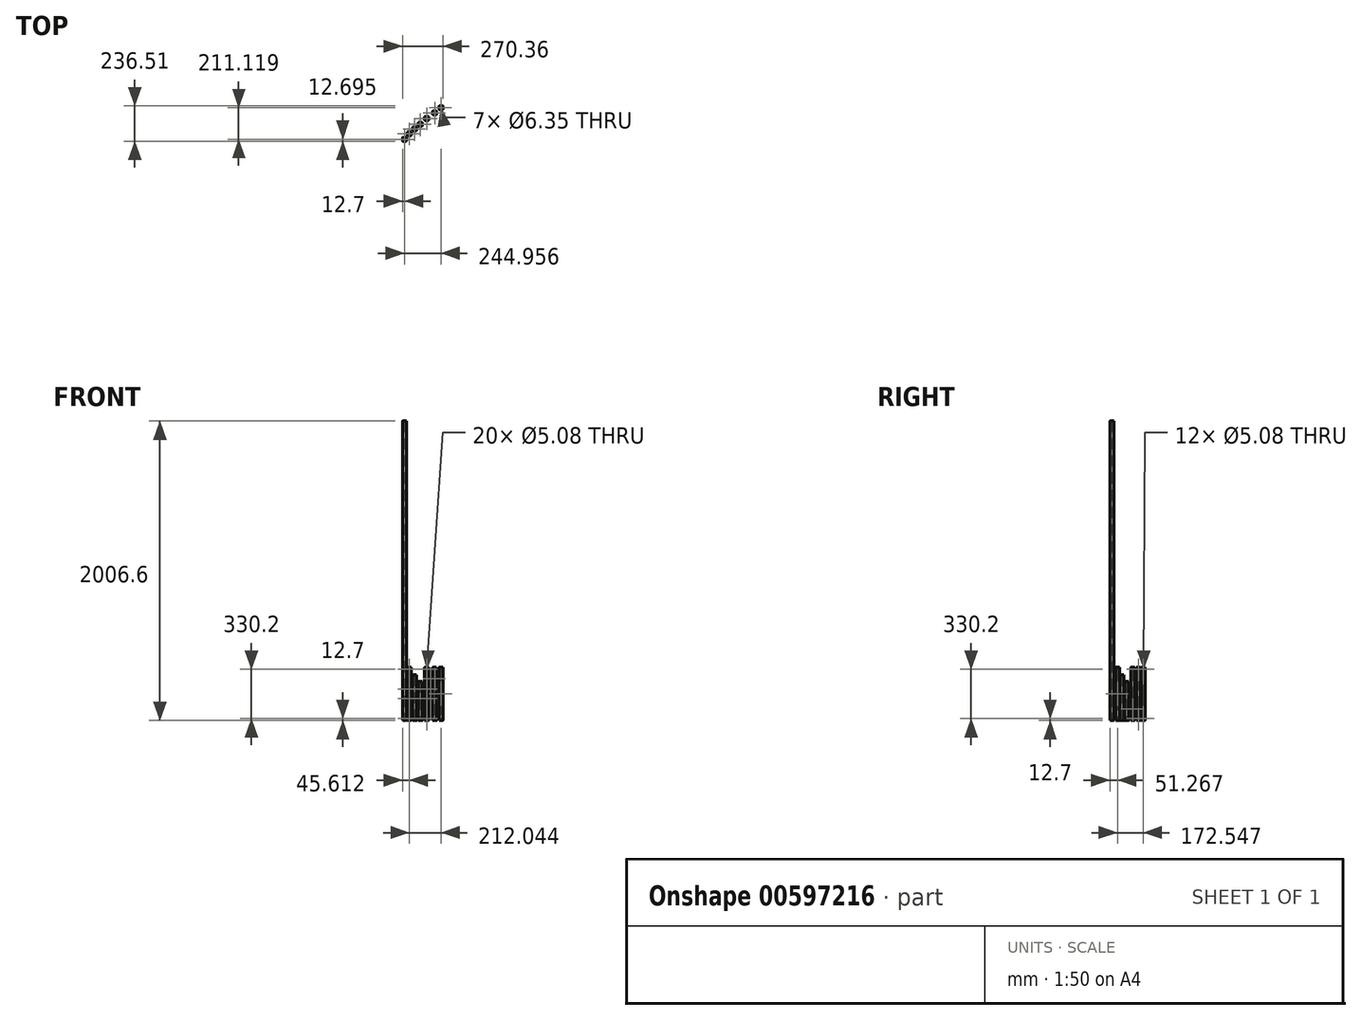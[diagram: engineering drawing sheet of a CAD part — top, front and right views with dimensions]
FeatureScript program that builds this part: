
annotation { "Feature Type Name" : "Feature", "Feature Type Description" : "" }
export const myFeature = defineFeature(function(context is Context, id is Id, definition is map)
    precondition{}
    {
        {
            var Q0;
            Q0=qCreatedBy(makeId("Top.planeOp"),FACE);
            var sketch = newSketch(context, id + "F0", { "sketchPlane" : qUnion([Q0])});
            skLineSegment(sketch, "E0.bottom", {"start": v(-80.08, 31.14) * mm, "end": v(-100.4, 31.14) * mm});
            skLineSegment(sketch, "E0.top", {"start": v(-80.08, 5.74) * mm, "end": v(-100.4, 5.74) * mm});
            skLineSegment(sketch, "E0.left", {"start": v(-77.54, 28.6) * mm, "end": v(-77.54, 8.28) * mm});
            skLineSegment(sketch, "E0.right", {"start": v(-102.94, 28.6) * mm, "end": v(-102.94, 8.28) * mm});
            skPoint(sketch, "E0.middle", {"position": v(-90.24, 18.44) * mm});
            skPoint(sketch, "E1.visualSharp", {"position": v(-102.94, 31.14) * mm});
            skArc(sketch, "E1.filletArc", {"start": v(-100.4, 31.14) * mm, "mid": v(-102.2, 30.4) * mm, "end": v(-102.94, 28.6) * mm});
            skPoint(sketch, "E2.visualSharp", {"position": v(-102.94, 5.74) * mm});
            skArc(sketch, "E2.filletArc", {"start": v(-102.94, 8.28) * mm, "mid": v(-102.2, 6.48) * mm, "end": v(-100.4, 5.74) * mm});
            skPoint(sketch, "E3.visualSharp", {"position": v(-77.54, 5.74) * mm});
            skArc(sketch, "E3.filletArc", {"start": v(-80.08, 5.74) * mm, "mid": v(-78.28, 6.48) * mm, "end": v(-77.54, 8.28) * mm});
            skPoint(sketch, "E4.visualSharp", {"position": v(-77.54, 31.14) * mm});
            skArc(sketch, "E4.filletArc", {"start": v(-77.54, 28.6) * mm, "mid": v(-78.28, 30.4) * mm, "end": v(-80.08, 31.14) * mm});
            skCircle(sketch, "E5", {"center": v(-90.24, 18.44) * mm, "radius": 3.18 * mm});
            skSolve(sketch);
        }
        {
            var Q0;
            Q0=makeQuery(id+"F0.imprint","IMPRINT",FACE,{"disambiguationData":[TD([[makeQuery(id+"F0.imprint","IMPRINT",EDGE,{"derivedFrom":sQuery(id+"F0.wireOp",EDGE,"E0.bottom")}),1.0]])]});
            extrude(context, id + "F1", {"entities" : qUnion([Q0]), "depth" : 2006.6 * mm, "offsetDistance" : 25.4 * mm});
        }
        {
            var Q0;
            Q0=qCreatedBy(makeId("Top.planeOp"),FACE);
            var sketch = newSketch(context, id + "F2", { "sketchPlane" : qUnion([Q0])});
            skLineSegment(sketch, "E6.bottom", {"start": v(-47.17, 69.7) * mm, "end": v(-67.49, 69.7) * mm});
            skLineSegment(sketch, "E6.top", {"start": v(-47.17, 44.3) * mm, "end": v(-67.49, 44.3) * mm});
            skLineSegment(sketch, "E6.left", {"start": v(-44.63, 67.17) * mm, "end": v(-44.63, 46.85) * mm});
            skLineSegment(sketch, "E6.right", {"start": v(-70.03, 67.17) * mm, "end": v(-70.03, 46.85) * mm});
            skPoint(sketch, "E6.middle", {"position": v(-57.33, 57) * mm});
            skPoint(sketch, "E7.visualSharp", {"position": v(-70.03, 69.7) * mm});
            skArc(sketch, "E7.filletArc", {"start": v(-67.49, 69.7) * mm, "mid": v(-69.28, 68.96) * mm, "end": v(-70.03, 67.17) * mm});
            skPoint(sketch, "E8.visualSharp", {"position": v(-70.03, 44.3) * mm});
            skArc(sketch, "E8.filletArc", {"start": v(-70.03, 46.85) * mm, "mid": v(-69.28, 45.05) * mm, "end": v(-67.49, 44.3) * mm});
            skPoint(sketch, "E9.visualSharp", {"position": v(-44.63, 44.3) * mm});
            skArc(sketch, "E9.filletArc", {"start": v(-47.17, 44.3) * mm, "mid": v(-45.37, 45.05) * mm, "end": v(-44.63, 46.85) * mm});
            skPoint(sketch, "E10.visualSharp", {"position": v(-44.63, 69.7) * mm});
            skArc(sketch, "E10.filletArc", {"start": v(-44.63, 67.17) * mm, "mid": v(-45.37, 68.96) * mm, "end": v(-47.17, 69.7) * mm});
            skCircle(sketch, "E11", {"center": v(-57.33, 57) * mm, "radius": 3.18 * mm});
            skSolve(sketch);
        }
        {
            var Q0;
            Q0 = qSketchRegion(id + "F2", true);
            extrude(context, id + "F3", {"entities" : qUnion([Q0]), "depth" : 355.6 * mm, "offsetDistance" : 25.4 * mm});
        }
        {
            var Q0;
            Q0=qCreatedBy(makeId("Top.planeOp"),FACE);
            var sketch = newSketch(context, id + "F4", { "sketchPlane" : qUnion([Q0])});
            skLineSegment(sketch, "E12.bottom", {"start": v(-11.92, 100.84) * mm, "end": v(-32.24, 100.84) * mm});
            skLineSegment(sketch, "E12.top", {"start": v(-11.92, 75.44) * mm, "end": v(-32.24, 75.44) * mm});
            skLineSegment(sketch, "E12.left", {"start": v(-9.38, 98.3) * mm, "end": v(-9.38, 77.98) * mm});
            skLineSegment(sketch, "E12.right", {"start": v(-34.78, 98.3) * mm, "end": v(-34.78, 77.98) * mm});
            skPoint(sketch, "E12.middle", {"position": v(-22.08, 88.14) * mm});
            skPoint(sketch, "E13.visualSharp", {"position": v(-34.78, 100.84) * mm});
            skArc(sketch, "E13.filletArc", {"start": v(-32.24, 100.84) * mm, "mid": v(-34.04, 100.1) * mm, "end": v(-34.78, 98.3) * mm});
            skPoint(sketch, "E14.visualSharp", {"position": v(-34.78, 75.44) * mm});
            skArc(sketch, "E14.filletArc", {"start": v(-34.78, 77.98) * mm, "mid": v(-34.04, 76.18) * mm, "end": v(-32.24, 75.44) * mm});
            skPoint(sketch, "E15.visualSharp", {"position": v(-9.38, 75.44) * mm});
            skArc(sketch, "E15.filletArc", {"start": v(-11.92, 75.44) * mm, "mid": v(-10.13, 76.18) * mm, "end": v(-9.38, 77.98) * mm});
            skPoint(sketch, "E16.visualSharp", {"position": v(-9.38, 100.84) * mm});
            skArc(sketch, "E16.filletArc", {"start": v(-9.38, 98.3) * mm, "mid": v(-10.13, 100.1) * mm, "end": v(-11.92, 100.84) * mm});
            skCircle(sketch, "E17", {"center": v(-22.08, 88.14) * mm, "radius": 3.18 * mm});
            skSolve(sketch);
        }
        {
            var Q0;
            Q0 = qSketchRegion(id + "F4", true);
            extrude(context, id + "F5", {"entities" : qUnion([Q0]), "depth" : 304.8 * mm, "offsetDistance" : 25.4 * mm});
        }
        {
            var Q0;
            Q0=qCreatedBy(makeId("Top.planeOp"),FACE);
            var sketch = newSketch(context, id + "F6", { "sketchPlane" : qUnion([Q0])});
            skLineSegment(sketch, "E18.bottom", {"start": v(27.14, 131.97) * mm, "end": v(6.82, 131.97) * mm});
            skLineSegment(sketch, "E18.top", {"start": v(27.14, 106.57) * mm, "end": v(6.82, 106.57) * mm});
            skLineSegment(sketch, "E18.left", {"start": v(29.68, 129.43) * mm, "end": v(29.68, 109.1) * mm});
            skLineSegment(sketch, "E18.right", {"start": v(4.28, 129.43) * mm, "end": v(4.28, 109.1) * mm});
            skPoint(sketch, "E18.middle", {"position": v(16.98, 119.27) * mm});
            skPoint(sketch, "E19.visualSharp", {"position": v(4.28, 131.97) * mm});
            skArc(sketch, "E19.filletArc", {"start": v(6.82, 131.97) * mm, "mid": v(5.02, 131.23) * mm, "end": v(4.28, 129.43) * mm});
            skPoint(sketch, "E20.visualSharp", {"position": v(4.28, 106.57) * mm});
            skArc(sketch, "E20.filletArc", {"start": v(4.28, 109.1) * mm, "mid": v(5.02, 107.31) * mm, "end": v(6.82, 106.57) * mm});
            skPoint(sketch, "E21.visualSharp", {"position": v(29.68, 106.57) * mm});
            skArc(sketch, "E21.filletArc", {"start": v(27.14, 106.57) * mm, "mid": v(28.93, 107.31) * mm, "end": v(29.68, 109.1) * mm});
            skPoint(sketch, "E22.visualSharp", {"position": v(29.68, 131.97) * mm});
            skArc(sketch, "E22.filletArc", {"start": v(29.68, 129.43) * mm, "mid": v(28.93, 131.23) * mm, "end": v(27.14, 131.97) * mm});
            skCircle(sketch, "E23", {"center": v(16.98, 119.27) * mm, "radius": 3.18 * mm});
            skSolve(sketch);
        }
        {
            var Q0;
            Q0 = qSketchRegion(id + "F6", true);
            extrude(context, id + "F7", {"entities" : qUnion([Q0]), "depth" : 260.35 * mm, "offsetDistance" : 25.4 * mm});
        }
        {
            var Q0;
            Q0=qCreatedBy(makeId("Top.planeOp"),FACE);
            var sketch = newSketch(context, id + "F8", { "sketchPlane" : qUnion([Q0])});
            skLineSegment(sketch, "E24.bottom", {"start": v(68.72, 171.36) * mm, "end": v(48.4, 171.36) * mm});
            skLineSegment(sketch, "E24.top", {"start": v(68.72, 145.96) * mm, "end": v(48.4, 145.96) * mm});
            skLineSegment(sketch, "E24.left", {"start": v(71.26, 168.82) * mm, "end": v(71.26, 148.5) * mm});
            skLineSegment(sketch, "E24.right", {"start": v(45.86, 168.82) * mm, "end": v(45.86, 148.5) * mm});
            skPoint(sketch, "E24.middle", {"position": v(58.56, 158.66) * mm});
            skPoint(sketch, "E25.visualSharp", {"position": v(45.86, 171.36) * mm});
            skArc(sketch, "E25.filletArc", {"start": v(48.4, 171.36) * mm, "mid": v(46.6, 170.62) * mm, "end": v(45.86, 168.82) * mm});
            skPoint(sketch, "E26.visualSharp", {"position": v(45.86, 145.96) * mm});
            skArc(sketch, "E26.filletArc", {"start": v(45.86, 148.5) * mm, "mid": v(46.6, 146.7) * mm, "end": v(48.4, 145.96) * mm});
            skPoint(sketch, "E27.visualSharp", {"position": v(71.26, 145.96) * mm});
            skArc(sketch, "E27.filletArc", {"start": v(68.72, 145.96) * mm, "mid": v(70.52, 146.7) * mm, "end": v(71.26, 148.5) * mm});
            skPoint(sketch, "E28.visualSharp", {"position": v(71.26, 171.36) * mm});
            skArc(sketch, "E28.filletArc", {"start": v(71.26, 168.82) * mm, "mid": v(70.52, 170.62) * mm, "end": v(68.72, 171.36) * mm});
            skCircle(sketch, "E29", {"center": v(58.56, 158.66) * mm, "radius": 3.18 * mm});
            skSolve(sketch);
        }
        {
            var Q0;
            Q0 = qSketchRegion(id + "F8", true);
            extrude(context, id + "F9", {"entities" : qUnion([Q0]), "depth" : 355.6 * mm, "offsetDistance" : 25.4 * mm});
        }
        {
            var Q0;
            Q0=makeQuery(id+"F9.opExtrude","SWEPT_FACE",FACE,{"disambiguationData":[OSD([sQuery(id+"F8.wireOp",EDGE,"E24.left")])]});
            var sketch = newSketch(context, id + "F10", { "sketchPlane" : qUnion([Q0])});
            skLineSegment(sketch, "E30", {"start": v(158.66, 0) * mm, "end": v(158.66, 76.2) * mm, "construction": true});
            skCircle(sketch, "E31", {"center": v(158.66, 76.2) * mm, "radius": 2.54 * mm});
            skSolve(sketch);
        }
        {
            var Q0;
            Q0 = qSketchRegion(id + "F10", true);
            extrude(context, id + "F11", {"entities" : qUnion([Q0]), "operationType" : NewBodyOperationType.REMOVE, "oppositeDirection" : true, "depth" : 25.4 * mm, "offsetDistance" : 25.4 * mm});
        }
        {
            var Q0;
            Q0=makeQuery(id+"F9.opExtrude","SWEPT_FACE",FACE,{"disambiguationData":[OSD([sQuery(id+"F8.wireOp",EDGE,"E24.top")])]});
            var sketch = newSketch(context, id + "F12", { "sketchPlane" : qUnion([Q0])});
            skLineSegment(sketch, "E32", {"start": v(48.4, 177.8) * mm, "end": v(68.72, 177.8) * mm, "construction": true});
            skLineSegment(sketch, "E33", {"start": v(58.56, 177.8) * mm, "end": v(58.56, 209.55) * mm, "construction": true});
            skLineSegment(sketch, "E34", {"start": v(58.56, 177.8) * mm, "end": v(58.56, 146.05) * mm, "construction": true});
            skCircle(sketch, "E35", {"center": v(58.56, 209.55) * mm, "radius": 2.54 * mm});
            skCircle(sketch, "E36", {"center": v(58.56, 146.05) * mm, "radius": 2.54 * mm});
            skLineSegment(sketch, "E37", {"start": v(58.56, 355.6) * mm, "end": v(58.56, 342.9) * mm, "construction": true});
            skLineSegment(sketch, "E38", {"start": v(58.56, 0) * mm, "end": v(58.56, 12.7) * mm, "construction": true});
            skCircle(sketch, "E39", {"center": v(58.56, 12.7) * mm, "radius": 2.54 * mm});
            skCircle(sketch, "E40", {"center": v(58.56, 342.9) * mm, "radius": 2.54 * mm});
            skSolve(sketch);
        }
        {
            var Q0;
            Q0 = qSketchRegion(id + "F12", true);
            extrude(context, id + "F13", {"entities" : qUnion([Q0]), "operationType" : NewBodyOperationType.REMOVE, "oppositeDirection" : true, "depth" : 25.4 * mm, "offsetDistance" : 25.4 * mm});
        }
        {
            var Q0;
            Q0=makeQuery(id+"F3.opExtrude","SWEPT_FACE",FACE,{"disambiguationData":[OSD([sQuery(id+"F2.wireOp",EDGE,"E6.top")])]});
            var sketch = newSketch(context, id + "F14", { "sketchPlane" : qUnion([Q0])});
            skLineSegment(sketch, "E41", {"start": v(-57.33, 355.6) * mm, "end": v(-57.33, 342.9) * mm, "construction": true});
            skCircle(sketch, "E42", {"center": v(-57.33, 342.9) * mm, "radius": 2.54 * mm});
            skLineSegment(sketch, "E43", {"start": v(-57.33, 0) * mm, "end": v(-57.33, 12.7) * mm, "construction": true});
            skLineSegment(sketch, "E44", {"start": v(-67.49, 177.8) * mm, "end": v(-47.17, 177.8) * mm, "construction": true});
            skLineSegment(sketch, "E45", {"start": v(-57.33, 177.8) * mm, "end": v(-57.33, 209.55) * mm, "construction": true});
            skLineSegment(sketch, "E46", {"start": v(-57.33, 177.8) * mm, "end": v(-57.33, 146.05) * mm, "construction": true});
            skCircle(sketch, "E47", {"center": v(-57.33, 146.05) * mm, "radius": 2.54 * mm});
            skCircle(sketch, "E48", {"center": v(-57.33, 209.55) * mm, "radius": 2.54 * mm});
            skCircle(sketch, "E49", {"center": v(-57.33, 12.7) * mm, "radius": 2.54 * mm});
            skSolve(sketch);
        }
        {
            var Q0;
            Q0 = qSketchRegion(id + "F14", true);
            extrude(context, id + "F15", {"entities" : qUnion([Q0]), "operationType" : NewBodyOperationType.REMOVE, "oppositeDirection" : true, "depth" : 25.4 * mm, "offsetDistance" : 25.4 * mm});
        }
        {
            var Q0;
            Q0=makeQuery(id+"F3.opExtrude","SWEPT_FACE",FACE,{"disambiguationData":[OSD([sQuery(id+"F2.wireOp",EDGE,"E6.left")])]});
            var sketch = newSketch(context, id + "F16", { "sketchPlane" : qUnion([Q0])});
            skLineSegment(sketch, "E50", {"start": v(46.85, 177.8) * mm, "end": v(67.17, 177.8) * mm, "construction": true});
            skCircle(sketch, "E51", {"center": v(57, 177.8) * mm, "radius": 2.54 * mm});
            skSolve(sketch);
        }
        {
            var Q0;
            Q0 = qSketchRegion(id + "F16", true);
            extrude(context, id + "F17", {"entities" : qUnion([Q0]), "operationType" : NewBodyOperationType.REMOVE, "oppositeDirection" : true, "depth" : 25.4 * mm, "offsetDistance" : 25.4 * mm});
        }
        {
            var Q0;
            Q0=qCreatedBy(makeId("Top.planeOp"),FACE);
            var sketch = newSketch(context, id + "F18", { "sketchPlane" : qUnion([Q0])});
            skLineSegment(sketch, "E52.bottom", {"start": v(122.64, 209.06) * mm, "end": v(102.32, 209.06) * mm});
            skLineSegment(sketch, "E52.top", {"start": v(122.64, 183.66) * mm, "end": v(102.32, 183.66) * mm});
            skLineSegment(sketch, "E52.left", {"start": v(125.18, 206.52) * mm, "end": v(125.18, 186.2) * mm});
            skLineSegment(sketch, "E52.right", {"start": v(99.78, 206.52) * mm, "end": v(99.78, 186.2) * mm});
            skPoint(sketch, "E52.middle", {"position": v(112.48, 196.36) * mm});
            skPoint(sketch, "E53.visualSharp", {"position": v(99.78, 209.06) * mm});
            skArc(sketch, "E53.filletArc", {"start": v(102.32, 209.06) * mm, "mid": v(100.53, 208.31) * mm, "end": v(99.78, 206.52) * mm});
            skPoint(sketch, "E54.visualSharp", {"position": v(99.78, 183.66) * mm});
            skArc(sketch, "E54.filletArc", {"start": v(99.78, 186.2) * mm, "mid": v(100.53, 184.4) * mm, "end": v(102.32, 183.66) * mm});
            skPoint(sketch, "E55.visualSharp", {"position": v(125.18, 183.66) * mm});
            skArc(sketch, "E55.filletArc", {"start": v(122.64, 183.66) * mm, "mid": v(124.44, 184.4) * mm, "end": v(125.18, 186.2) * mm});
            skPoint(sketch, "E56.visualSharp", {"position": v(125.18, 209.06) * mm});
            skArc(sketch, "E56.filletArc", {"start": v(125.18, 206.52) * mm, "mid": v(124.44, 208.31) * mm, "end": v(122.64, 209.06) * mm});
            skCircle(sketch, "E57", {"center": v(112.48, 196.36) * mm, "radius": 3.18 * mm});
            skSolve(sketch);
        }
        {
            var Q0;
            Q0 = qSketchRegion(id + "F18", true);
            extrude(context, id + "F19", {"entities" : qUnion([Q0]), "depth" : 355.6 * mm, "offsetDistance" : 25.4 * mm});
        }
        {
            var Q0;
            Q0=qCreatedBy(makeId("Top.planeOp"),FACE);
            var sketch = newSketch(context, id + "F20", { "sketchPlane" : qUnion([Q0])});
            skLineSegment(sketch, "E58.bottom", {"start": v(164.88, 242.25) * mm, "end": v(144.56, 242.25) * mm});
            skLineSegment(sketch, "E58.top", {"start": v(164.88, 216.85) * mm, "end": v(144.56, 216.85) * mm});
            skLineSegment(sketch, "E58.left", {"start": v(167.42, 239.71) * mm, "end": v(167.42, 219.4) * mm});
            skLineSegment(sketch, "E58.right", {"start": v(142.02, 239.71) * mm, "end": v(142.02, 219.4) * mm});
            skPoint(sketch, "E58.middle", {"position": v(154.72, 229.55) * mm});
            skPoint(sketch, "E59.visualSharp", {"position": v(142.02, 242.25) * mm});
            skArc(sketch, "E59.filletArc", {"start": v(144.56, 242.25) * mm, "mid": v(142.76, 241.5) * mm, "end": v(142.02, 239.71) * mm});
            skPoint(sketch, "E60.visualSharp", {"position": v(142.02, 216.85) * mm});
            skArc(sketch, "E60.filletArc", {"start": v(142.02, 219.4) * mm, "mid": v(142.76, 217.6) * mm, "end": v(144.56, 216.85) * mm});
            skPoint(sketch, "E61.visualSharp", {"position": v(167.42, 216.85) * mm});
            skArc(sketch, "E61.filletArc", {"start": v(164.88, 216.85) * mm, "mid": v(166.67, 217.6) * mm, "end": v(167.42, 219.4) * mm});
            skPoint(sketch, "E62.visualSharp", {"position": v(167.42, 242.25) * mm});
            skArc(sketch, "E62.filletArc", {"start": v(167.42, 239.71) * mm, "mid": v(166.67, 241.5) * mm, "end": v(164.88, 242.25) * mm});
            skCircle(sketch, "E63", {"center": v(154.72, 229.55) * mm, "radius": 3.18 * mm});
            skSolve(sketch);
        }
        {
            var Q0;
            Q0 = qSketchRegion(id + "F20", true);
            extrude(context, id + "F21", {"entities" : qUnion([Q0]), "depth" : 355.6 * mm, "offsetDistance" : 25.4 * mm});
        }
        {
            var Q0;
            Q0=makeQuery(id+"F19.opExtrude","SWEPT_FACE",FACE,{"disambiguationData":[OSD([sQuery(id+"F18.wireOp",EDGE,"E52.top")])]});
            var sketch = newSketch(context, id + "F22", { "sketchPlane" : qUnion([Q0])});
            skLineSegment(sketch, "E64", {"start": v(112.48, 355.6) * mm, "end": v(112.48, 279.4) * mm, "construction": true});
            skCircle(sketch, "E65", {"center": v(112.48, 279.4) * mm, "radius": 2.54 * mm});
            skSolve(sketch);
        }
        {
            var Q0;
            Q0 = qSketchRegion(id + "F22", true);
            extrude(context, id + "F23", {"entities" : qUnion([Q0]), "operationType" : NewBodyOperationType.REMOVE, "oppositeDirection" : true, "depth" : 25.4 * mm, "offsetDistance" : 25.4 * mm});
        }
        {
            var Q0;
            Q0=makeQuery(id+"F19.opExtrude","SWEPT_FACE",FACE,{"disambiguationData":[OSD([sQuery(id+"F18.wireOp",EDGE,"E52.left")])]});
            var sketch = newSketch(context, id + "F24", { "sketchPlane" : qUnion([Q0])});
            skLineSegment(sketch, "E66", {"start": v(196.36, 355.6) * mm, "end": v(196.36, 342.9) * mm, "construction": true});
            skLineSegment(sketch, "E67", {"start": v(196.36, 0) * mm, "end": v(196.36, 12.7) * mm, "construction": true});
            skCircle(sketch, "E68", {"center": v(196.36, 12.7) * mm, "radius": 2.54 * mm});
            skCircle(sketch, "E69", {"center": v(196.36, 342.9) * mm, "radius": 2.54 * mm});
            skSolve(sketch);
        }
        {
            var Q0;
            Q0 = qSketchRegion(id + "F24", true);
            extrude(context, id + "F25", {"entities" : qUnion([Q0]), "operationType" : NewBodyOperationType.REMOVE, "oppositeDirection" : true, "depth" : 25.4 * mm, "offsetDistance" : 25.4 * mm});
        }
        {
            var Q0;
            Q0=makeQuery(id+"F21.opExtrude","SWEPT_FACE",FACE,{"disambiguationData":[OSD([sQuery(id+"F20.wireOp",EDGE,"E58.left")])]});
            var sketch = newSketch(context, id + "F26", { "sketchPlane" : qUnion([Q0])});
            skLineSegment(sketch, "E70", {"start": v(229.55, 355.6) * mm, "end": v(229.55, 342.9) * mm, "construction": true});
            skLineSegment(sketch, "E71", {"start": v(229.55, 0) * mm, "end": v(229.55, 12.7) * mm, "construction": true});
            skCircle(sketch, "E72", {"center": v(229.55, 12.7) * mm, "radius": 2.54 * mm});
            skCircle(sketch, "E73", {"center": v(229.55, 342.9) * mm, "radius": 2.54 * mm});
            skSolve(sketch);
        }
        {
            var Q0;
            Q0 = qSketchRegion(id + "F26", true);
            extrude(context, id + "F27", {"entities" : qUnion([Q0]), "operationType" : NewBodyOperationType.REMOVE, "oppositeDirection" : true, "depth" : 25.4 * mm, "offsetDistance" : 25.4 * mm});
        }
        {
            var Q0;
            Q0=makeQuery(id+"F21.opExtrude","SWEPT_FACE",FACE,{"disambiguationData":[OSD([sQuery(id+"F20.wireOp",EDGE,"E58.top")])]});
            var sketch = newSketch(context, id + "F28", { "sketchPlane" : qUnion([Q0])});
            skLineSegment(sketch, "E74", {"start": v(154.72, 355.6) * mm, "end": v(154.72, 177.8) * mm, "construction": true});
            skCircle(sketch, "E75", {"center": v(154.72, 177.8) * mm, "radius": 2.54 * mm});
            skSolve(sketch);
        }
        {
            var Q0;
            Q0 = qSketchRegion(id + "F28", true);
            extrude(context, id + "F29", {"entities" : qUnion([Q0]), "operationType" : NewBodyOperationType.REMOVE, "oppositeDirection" : true, "depth" : 25.4 * mm, "offsetDistance" : 25.4 * mm});
        }
    });
